# Revit family: EKF_EE_БоковыеОснованияСейсмоцоколя(2шт)Trivia_AVERES
name_source: partatom
category: Электрооборудование
units: mm (PartAtom-declared; Revit-internal decimal feet)

## family parameters
Всегда вертикально = Нет
На основе рабочей плоскости = Да
Общий = Да
При загрузке вырезать с полостями = Нет
Размер круглого соединителя = Использовать диаметр
Тип детали = Силовой щит
Точка расчета площади = Нет

## types (1)
- 2 боковых основания сейсмоцоколя Г600 мм EKF AVERES
    ADSK_Единица измерения = шт.
    ADSK_Завод-изготовитель = EKF
    ADSK_Код изделия = BSP600SR
    ADSK_Количество = 1
    ADSK_Марка = 2 боковых основания сейсмоцоколя Г600 мм EKF AVERES
    ADSK_Масса = 0
    ADSK_Материал = RAL 7035_Сталь
    ADSK_Наименование = 2 боковых основания сейсмоцоколя Г600 мм EKF AVERES
    ADSK_Обозначение = 2 боковых основания сейсмоцоколя Г600 мм EKF AVERES
    ADSK_Размер_Высота = 100 мм
    ADSK_Размер_Глубина = 65 мм
    ADSK_Размер_Ширина = 610 мм
    Изготовитель = EKF
    Отметка по умолчанию = 1219.2 мм
    Серия номенклатуры = Averes
    Степень защиты IP = -
    ТВ = EKF_2_TRIVIA_AVERES
    Тип = 751 мм
    Тип установки = -
